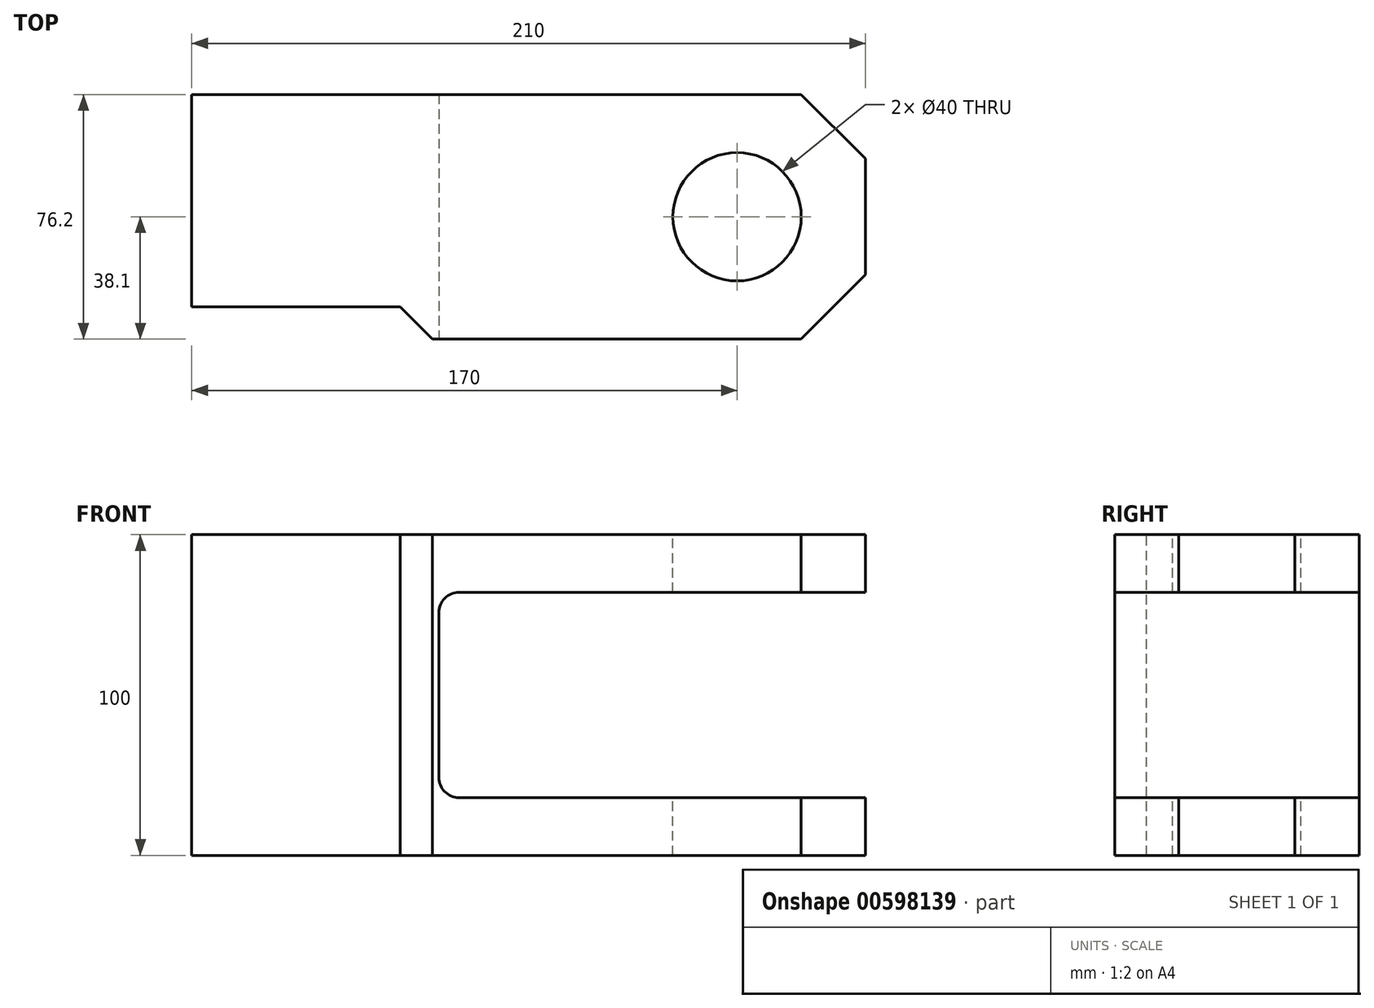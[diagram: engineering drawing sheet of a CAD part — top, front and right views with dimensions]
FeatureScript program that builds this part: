
annotation { "Feature Type Name" : "Feature", "Feature Type Description" : "" }
export const myFeature = defineFeature(function(context is Context, id is Id, definition is map)
    precondition{}
    {
        {
            var Q0;
            Q0=qCreatedBy(makeId("Front.planeOp"),FACE);
            var sketch = newSketch(context, id + "F0", { "sketchPlane" : qUnion([Q0])});
            skLineSegment(sketch, "E0.bottom", {"start": v(0, 0) * mm, "end": v(210, 0) * mm});
            skLineSegment(sketch, "E0.top", {"start": v(0, 100) * mm, "end": v(210, 100) * mm});
            skLineSegment(sketch, "E0.left", {"start": v(0, 0) * mm, "end": v(0, 100) * mm});
            skLineSegment(sketch, "E0.right", {"start": v(210, 0) * mm, "end": v(210, 100) * mm});
            skSolve(sketch);
        }
        {
            var Q0;
            Q0 = qSketchRegion(id + "F0", true);
            extrude(context, id + "F1", {"entities" : qUnion([Q0]), "depth" : 76.2 * mm, "offsetDistance" : 25.4 * mm});
        }
        {
            var Q0;
            Q0=makeQuery(id+"F1.opExtrude","CAP_FACE",FACE,{"disambiguationData":[OSD([sQuery(id+"F0.wireOp",EDGE,"E0.bottom"),sQuery(id+"F0.wireOp",EDGE,"E0.top"),sQuery(id+"F0.wireOp",EDGE,"E0.left"),sQuery(id+"F0.wireOp",EDGE,"E0.right")])],"isStart":false});
            var sketch = newSketch(context, id + "F2", { "sketchPlane" : qUnion([Q0])});
            skLineSegment(sketch, "E1.bottom", {"start": v(210, 82) * mm, "end": v(77, 82) * mm});
            skLineSegment(sketch, "E1.top", {"start": v(210, 18) * mm, "end": v(77, 18) * mm});
            skLineSegment(sketch, "E1.left", {"start": v(210, 82) * mm, "end": v(210, 18) * mm});
            skLineSegment(sketch, "E1.right", {"start": v(77, 82) * mm, "end": v(77, 18) * mm});
            skSolve(sketch);
        }
        {
            var Q0;
            Q0 = qSketchRegion(id + "F2", true);
            extrude(context, id + "F3", {"entities" : qUnion([Q0]), "operationType" : NewBodyOperationType.REMOVE, "endBound" : BoundingType.THROUGH_ALL, "oppositeDirection" : true, "depth" : 25.4 * mm, "offsetDistance" : 25.4 * mm});
        }
        {
            var Q0;
            Q0=makeQuery(id+"F3.boolean.opBoolean","COPY",EDGE,{"derivedFrom":makeQuery(id+"F3.opExtrude","SWEPT_EDGE",EDGE,{"disambiguationData":[OSD([sQuery(id+"F2.wireOp",EDGE,"E1.bottom"),sQuery(id+"F2.wireOp",EDGE,"E1.right")])]})});
            var Q1;
            Q1=makeQuery(id+"F3.boolean.opBoolean","COPY",EDGE,{"derivedFrom":makeQuery(id+"F3.opExtrude","SWEPT_EDGE",EDGE,{"disambiguationData":[OSD([sQuery(id+"F2.wireOp",EDGE,"E1.top"),sQuery(id+"F2.wireOp",EDGE,"E1.right")])]})});
            fillet(context, id + "F4", {"entities" : qUnion([Q0, Q1]), "radius" : 6.35 * mm, "tangentPropagation" : true, "allowEdgeOverflow" : false});
        }
        {
            var Q0;
            Q0=makeQuery(id+"F1.opExtrude","SWEPT_FACE",FACE,{"disambiguationData":[OSD([sQuery(id+"F0.wireOp",EDGE,"E0.top")])]});
            var sketch = newSketch(context, id + "F5", { "sketchPlane" : qUnion([Q0])});
            skLineSegment(sketch, "E2", {"start": v(190, 0) * mm, "end": v(210, -20) * mm});
            skLineSegment(sketch, "E3", {"start": v(210, -20) * mm, "end": v(210, -56.2) * mm});
            skLineSegment(sketch, "E4", {"start": v(210, -56.2) * mm, "end": v(190, -76.2) * mm});
            skLineSegment(sketch, "E5", {"start": v(190, -76.2) * mm, "end": v(190, -91.74) * mm});
            skLineSegment(sketch, "E6", {"start": v(190, -91.74) * mm, "end": v(258.7, -91.74) * mm});
            skLineSegment(sketch, "E7", {"start": v(258.7, -91.74) * mm, "end": v(258.7, 16.51) * mm});
            skLineSegment(sketch, "E8", {"start": v(258.7, 16.51) * mm, "end": v(190, 16.51) * mm});
            skLineSegment(sketch, "E9", {"start": v(190, 16.51) * mm, "end": v(190, 0) * mm});
            skCircle(sketch, "E10", {"center": v(170, -38.1) * mm, "radius": 20 * mm});
            skSolve(sketch);
        }
        {
            var Q0;
            Q0 = qSketchRegion(id + "F5", true);
            extrude(context, id + "F6", {"entities" : qUnion([Q0]), "operationType" : NewBodyOperationType.REMOVE, "endBound" : BoundingType.THROUGH_ALL, "oppositeDirection" : true, "depth" : 25.4 * mm, "offsetDistance" : 25.4 * mm});
        }
        {
            var Q0;
            Q0=makeQuery(id+"F1.opExtrude","SWEPT_FACE",FACE,{"disambiguationData":[OSD([sQuery(id+"F0.wireOp",EDGE,"E0.top")])]});
            var sketch = newSketch(context, id + "F7", { "sketchPlane" : qUnion([Q0])});
            skLineSegment(sketch, "E11", {"start": v(0, -66.2) * mm, "end": v(65, -66.2) * mm});
            skLineSegment(sketch, "E12", {"start": v(65, -66.2) * mm, "end": v(75, -76.2) * mm});
            skLineSegment(sketch, "E13", {"start": v(75, -76.2) * mm, "end": v(0, -76.2) * mm});
            skLineSegment(sketch, "E14", {"start": v(0, -76.2) * mm, "end": v(0, -66.2) * mm});
            skSolve(sketch);
        }
        {
            var Q0;
            Q0 = qSketchRegion(id + "F7", true);
            extrude(context, id + "F8", {"entities" : qUnion([Q0]), "operationType" : NewBodyOperationType.REMOVE, "endBound" : BoundingType.THROUGH_ALL, "oppositeDirection" : true, "depth" : 25.4 * mm, "offsetDistance" : 25.4 * mm});
        }
    });
